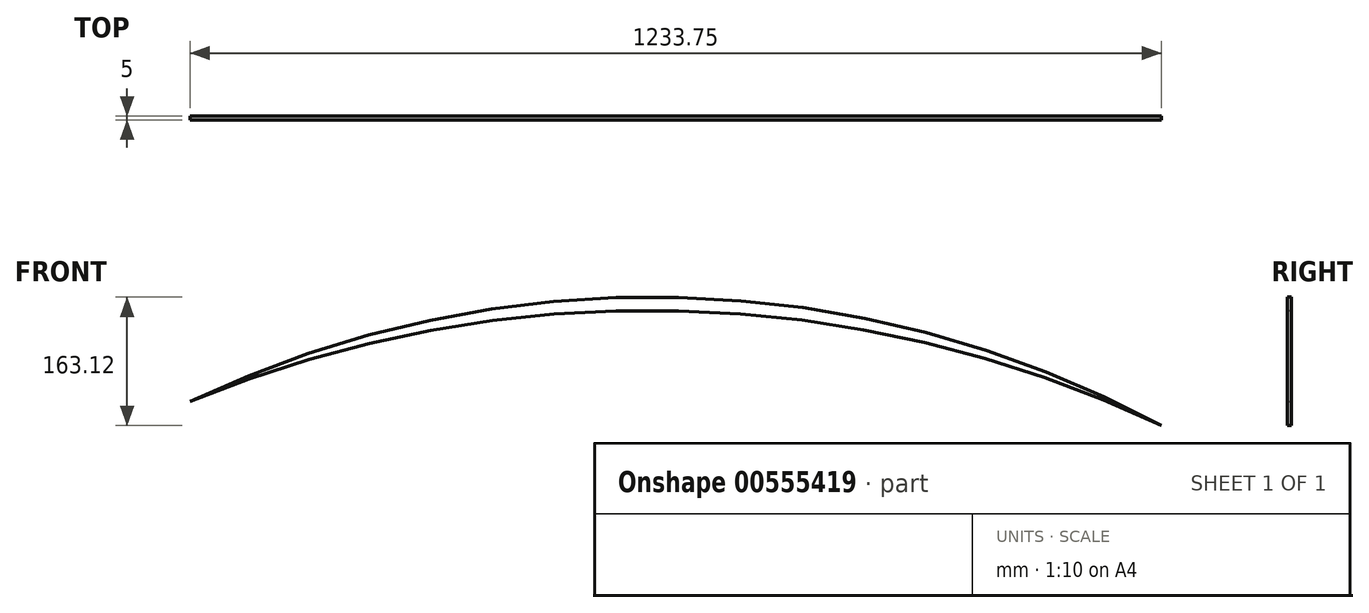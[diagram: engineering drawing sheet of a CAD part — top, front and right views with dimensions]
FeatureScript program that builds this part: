
annotation { "Feature Type Name" : "Feature", "Feature Type Description" : "" }
export const myFeature = defineFeature(function(context is Context, id is Id, definition is map)
    precondition{}
    {
        {
            var Q0;
            Q0=qCreatedBy(makeId("Front.planeOp"),FACE);
            var sketch = newSketch(context, id + "F0", { "sketchPlane" : qUnion([Q0])});
            skArc(sketch, "E0", {"start": v(568.46, 0) * mm, "mid": v(-44.8, 162.7) * mm, "end": v(-665.3, 30.27) * mm});
            skArc(sketch, "E1", {"start": v(568.46, 0) * mm, "mid": v(-45.21, 145.76) * mm, "end": v(-665.3, 30.27) * mm});
            skSolve(sketch);
        }
        {
            var Q0;
            Q0=makeQuery(id+"F0.imprint","IMPRINT",FACE,{"disambiguationData":[TD([[makeQuery(id+"F0.imprint","IMPRINT",EDGE,{"derivedFrom":sQuery(id+"F0.wireOp",EDGE,"E0")}),1.0]])]});
            extrude(context, id + "F1", {"entities" : qUnion([Q0]), "depth" : 5 * mm, "offsetDistance" : 25 * mm});
        }
    });
